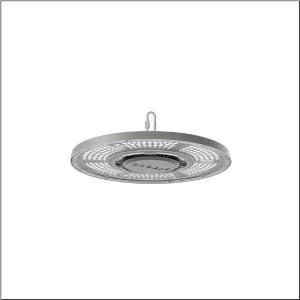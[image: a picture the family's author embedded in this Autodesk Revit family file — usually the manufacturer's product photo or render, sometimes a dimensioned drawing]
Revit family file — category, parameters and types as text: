
# Revit family: highbay_31-s_51hc427a4fmb
name_source: partatom
category: Lighting Fixtures
units: mm (PartAtom-declared; Revit-internal decimal feet)

## family parameters
Cut with Voids When Loaded = No
Host = Face
Light Source = No
Part Type = Normal
Room Calculation Point = No
Round Connector Dimension = Use Diameter
Shared = No

## types (1)
- Highbay 31-S (1 x LED, 14000 lm, 94 W, 4000K)
    Apparent Load = 94 VA
    CIE Flux Codes = 77 99 100 100 100
    Color Rendering = 80
    Color Temperature = 4000K
    Default Elevation = 1800 mm
    Description = Highbay 31-S, LED high bay luminaire, primary light control with lens, of PC, primary optical cover: cover panel, of PC, transparent, light emission: direct distribution, primary light characteristic: rotationally symmetric, installation type: suspended mounting, surface-mounted, LED, rated luminous flux: 14.000lm, luminous efficacy: 150lm/W, light colour: 840, colour temperature: 4000K, control gear: ECG, with cable, 3x 1.0mm², free wire ends, mains connection: 220..240V, AC/DC, 0/50..60Hz, cable length: 1,5m, rated input power: 94W, housing, rotationally symmetric, of diecast aluminium, powder-coated, grey aluminium (RAL 9007), with hook on luminaire side, incl. screw, diameter: 339mm, protection rating (complete): IP65, insulation class (complete): insulation class I (protective earthing), certification: CE, ENEC, UKCA, protection symbol: D, impact resistance: IK08, permissible operating ambient temperature: -30..+45°C, standard: EN 60598-2-22, EN 60598, corresponds to IFS (International Featured Standards) requirements for safety and quality in the food industry, packaging unit: 1 piece
    Height = 141 mm
    Lamp = 1 x LED
    Lamp Light Flux = 14000 lm
    Lamp Power = 94 W
    Lamp count = 1
    Length = 339 mm
    Luminous efficacy = 149 lm/W
    Manufacturer = Siteco
    ModVariant = No
    Model = 51HC427A4FMB
    Mounting Place = Ceiling
    Mounting Type = Pendant
    Number of Poles = 1
    OnlyDefault = Yes
    Power Factor = 1
    Product Name = Highbay 31-S
    Product group = LED high bay luminaire
    ProductGroupID = 903
    Protection Class = Protection class I
    Protection Degree = IP 65
    RLX_Detail_Level = 1
    RLX_Emergency_Light_Flux = 0 lm
    RLX_Emergency_Type = 0
    RLX_Emergency_Type_DB = No
    RlxData = <blob elided: 162437 chars, md5=9492afa2>
    Socket = socket
    Standby Power = 0 W
    System Light Flux = 14000 lm
    System Power = 94 W
    Type Comments = Product without accessories
    Type Image = l_1007237.jpg
    URL = http://relux.com
    VarID = ---
    Voltage = 0 V
    Weight = 0.00 kg
    Width = 0 mm  [stored 0 ft]

note: [stored X ft] marks values corroborated as IEEE doubles in the binary element streams (Revit-internal decimal feet)

## geometry (parser evidence)
native form markers: Blend x4, Sweep x11
no freeform markers — native parametric forms only
